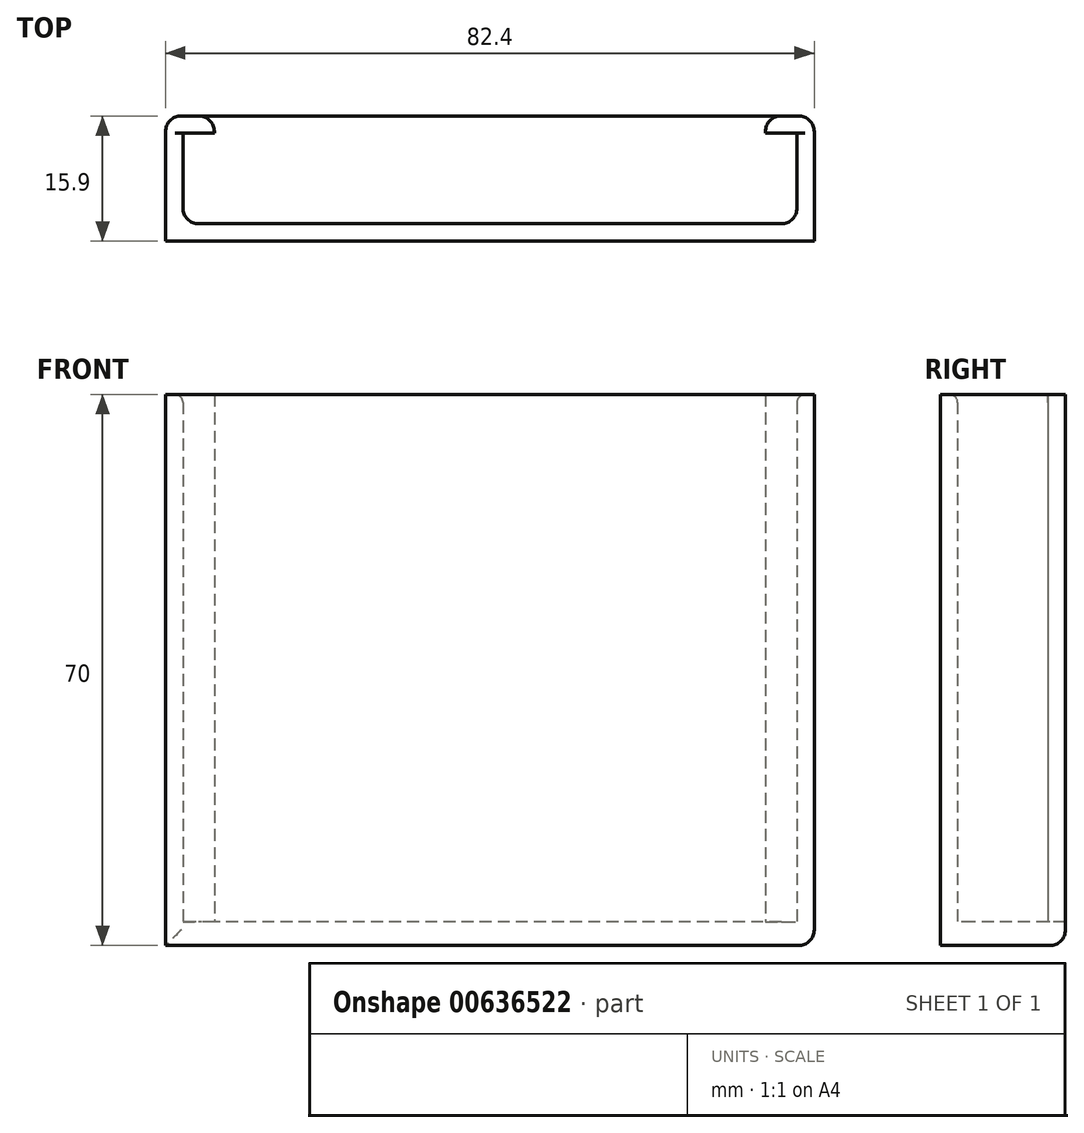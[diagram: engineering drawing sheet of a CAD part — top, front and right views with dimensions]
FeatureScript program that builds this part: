
annotation { "Feature Type Name" : "Feature", "Feature Type Description" : "" }
export const myFeature = defineFeature(function(context is Context, id is Id, definition is map)
    precondition{}
    {
        {
            var Q0;
            Q0=qCreatedBy(makeId("Top.planeOp"),FACE);
            var sketch = newSketch(context, id + "F0", { "sketchPlane" : qUnion([Q0])});
            skLineSegment(sketch, "E0", {"start": v(0, 7.22) * mm, "end": v(0, -7.47) * mm, "construction": true});
            skLineSegment(sketch, "E1", {"start": v(0, 0) * mm, "end": v(41.2, 0) * mm});
            skLineSegment(sketch, "E2", {"start": v(41.2, 0) * mm, "end": v(41.2, 15.9) * mm});
            skLineSegment(sketch, "E3", {"start": v(41.2, 15.9) * mm, "end": v(35, 15.9) * mm});
            skLineSegment(sketch, "E4", {"start": v(0, 2.2) * mm, "end": v(0, 0) * mm});
            skLineSegment(sketch, "E5.MirrorCS", {"start": v(-41.2, 0) * mm, "end": v(-41.2, 15.9) * mm});
            skLineSegment(sketch, "E6.MirrorCS", {"start": v(0, 0) * mm, "end": v(-41.2, 0) * mm});
            skLineSegment(sketch, "E7", {"start": v(35, 15.9) * mm, "end": v(35, 13.7) * mm});
            skLineSegment(sketch, "E8", {"start": v(35, 13.7) * mm, "end": v(39, 13.7) * mm});
            skLineSegment(sketch, "E9", {"start": v(39, 13.7) * mm, "end": v(39, 2.2) * mm});
            skLineSegment(sketch, "E10", {"start": v(39, 2.2) * mm, "end": v(0, 2.2) * mm});
            skLineSegment(sketch, "E11.MirrorCS", {"start": v(-39, 2.2) * mm, "end": v(0, 2.2) * mm});
            skLineSegment(sketch, "E12.MirrorCS", {"start": v(-39, 13.7) * mm, "end": v(-39, 2.2) * mm});
            skLineSegment(sketch, "E13.MirrorCS", {"start": v(-35, 13.7) * mm, "end": v(-39, 13.7) * mm});
            skLineSegment(sketch, "E14.MirrorCS", {"start": v(-35, 15.9) * mm, "end": v(-35, 13.7) * mm});
            skLineSegment(sketch, "E15.MirrorCS", {"start": v(-41.2, 15.9) * mm, "end": v(-35, 15.9) * mm});
            skLineSegment(sketch, "E16.top", {"start": v(-41.2, 0) * mm, "end": v(41.2, 0) * mm});
            skLineSegment(sketch, "E16.left", {"start": v(-41.2, 15.9) * mm, "end": v(-41.2, 0) * mm});
            skLineSegment(sketch, "E16.right", {"start": v(41.2, 14.6) * mm, "end": v(41.2, 0) * mm});
            skSolve(sketch);
        }
        {
            var Q0;
            Q0=makeQuery(id+"F0.imprint","IMPRINT",FACE,{"disambiguationData":[TD([[makeQuery(id+"F0.imprint","IMPRINT",EDGE,{"derivedFrom":sQuery(id+"F0.wireOp",EDGE,"E4")}),-1.0]])]});
            var Q1;
            Q1=makeQuery(id+"F0.imprint","IMPRINT",FACE,{"disambiguationData":[TD([[makeQuery(id+"F0.imprint","IMPRINT",EDGE,{"derivedFrom":sQuery(id+"F0.wireOp",EDGE,"E1")}),1.0]])]});
            var Q2;
            {var subQ1=sQuery(id+"F0.wireOp",EDGE,"E4");Q2=makeQuery(id+"F0.imprint","IMPRINT",FACE,{"disambiguationData":[TD([[makeQuery(id+"F0.imprint","IMPRINT",EDGE,{"derivedFrom":subQ1}),1.0]])]});}
            extrude(context, id + "F1", {"entities" : qUnion([Q0, Q1, Q2]), "depth" : 70 * mm});
        }
        {
            var Q0;
            {var subQ0=sQuery(id+"F0.wireOp",EDGE,"E4");Q0=makeQuery(id+"F0.imprint","IMPRINT",FACE,{"disambiguationData":[TD([[makeQuery(id+"F0.imprint","IMPRINT",EDGE,{"derivedFrom":subQ0}),-1.0]])]});}
            var sketch = newSketch(context, id + "F2", { "sketchPlane" : qUnion([Q0])});
            skLineSegment(sketch, "E17.bottom", {"start": v(41.2, 0) * mm, "end": v(-41.2, 0) * mm});
            skLineSegment(sketch, "E17.top", {"start": v(41.2, 15.9) * mm, "end": v(-41.2, 15.9) * mm});
            skLineSegment(sketch, "E17.left", {"start": v(41.2, 0) * mm, "end": v(41.2, 15.9) * mm});
            skLineSegment(sketch, "E17.right", {"start": v(-41.2, 0) * mm, "end": v(-41.2, 15.9) * mm});
            skSolve(sketch);
        }
        {
            var Q0;
            {var subQ1=sQuery(id+"F2.wireOp",EDGE,"E17.left");Q0=makeQuery(id+"F2.imprint","IMPRINT",FACE,{"disambiguationData":[TD([[makeQuery(id+"F2.imprint","IMPRINT",EDGE,{"derivedFrom":subQ1}),1.0]])]});}
            var Q1;
            {var subQ1=sQuery(id+"F2.wireOp",EDGE,"E17.right");Q1=makeQuery(id+"F2.imprint","IMPRINT",FACE,{"disambiguationData":[TD([[makeQuery(id+"F2.imprint","IMPRINT",EDGE,{"derivedFrom":subQ1}),1.0]])]});}
            extrude(context, id + "F3", {"entities" : qUnion([Q0, Q1]), "operationType" : NewBodyOperationType.ADD, "depth" : 3 * mm});
        }
        {
            var Q0;
            Q0=makeQuery(id+"F1.opExtrude","SWEPT_EDGE",EDGE,{"disambiguationData":[OSD([sQuery(id+"F0.wireOp",EDGE,"E16.top"),sQuery(id+"F0.wireOp",EDGE,"E16.right")])]});
            var Q1;
            Q1=makeQuery(id+"F1.opExtrude","SWEPT_EDGE",EDGE,{"disambiguationData":[OSD([sQuery(id+"F0.wireOp",EDGE,"E2"),sQuery(id+"F0.wireOp",EDGE,"E3")])]});
            var Q2;
            Q2=makeQuery(id+"F1.opExtrude","SWEPT_EDGE",EDGE,{"disambiguationData":[OSD([sQuery(id+"F0.wireOp",EDGE,"E3"),sQuery(id+"F0.wireOp",EDGE,"E7")])]});
            var Q3;
            Q3=makeQuery(id+"F1.opExtrude","SWEPT_EDGE",EDGE,{"disambiguationData":[OSD([sQuery(id+"F0.wireOp",EDGE,"E9"),sQuery(id+"F0.wireOp",EDGE,"E10")])]});
            var Q4;
            Q4=makeQuery(id+"F1.opExtrude","SWEPT_EDGE",EDGE,{"disambiguationData":[OSD([sQuery(id+"F0.wireOp",EDGE,"E14.MirrorCS"),sQuery(id+"F0.wireOp",EDGE,"E15.MirrorCS")])]});
            var Q5;
            Q5=makeQuery(id+"F1.opExtrude","SWEPT_EDGE",EDGE,{"disambiguationData":[OSD([sQuery(id+"F0.wireOp",EDGE,"E11.MirrorCS"),sQuery(id+"F0.wireOp",EDGE,"E12.MirrorCS")])]});
            var Q6;
            Q6=makeQuery(id+"F1.opExtrude","SWEPT_EDGE",EDGE,{"disambiguationData":[OSD([sQuery(id+"F0.wireOp",EDGE,"E15.MirrorCS"),sQuery(id+"F0.wireOp",EDGE,"E16.left")])]});
            var Q7;
            Q7=makeQuery(id+"F1.opExtrude","SWEPT_EDGE",EDGE,{"disambiguationData":[OSD([sQuery(id+"F0.wireOp",EDGE,"E16.top"),sQuery(id+"F0.wireOp",EDGE,"E16.left")])]});
            var Q8;
            Q8=makeQuery(id+"F1.opExtrude","CAP_EDGE",EDGE,{"disambiguationData":[OSD([sQuery(id+"F0.wireOp",EDGE,"E16.top")])],"isStart":true});
            var Q9;
            Q9=makeQuery(id+"F3.boolean.opBoolean","MERGE",EDGE,{"derivedFrom":[makeQuery(id+"F1.opExtrude","CAP_EDGE",EDGE,{"disambiguationData":[OSD([sQuery(id+"F0.wireOp",EDGE,"E3")])],"isStart":true}),makeQuery(id+"F1.opExtrude","CAP_EDGE",EDGE,{"disambiguationData":[OSD([sQuery(id+"F0.wireOp",EDGE,"E15.MirrorCS")])],"isStart":true}),makeQuery(id+"F3.opExtrude","CAP_EDGE",EDGE,{"disambiguationData":[OSD([sQuery(id+"F2.wireOp",EDGE,"E17.top")])],"isStart":true})]});
            var Q10;
            Q10=makeQuery(id+"F1.opExtrude","CAP_EDGE",EDGE,{"disambiguationData":[OSD([sQuery(id+"F0.wireOp",EDGE,"E16.left")])],"isStart":true});
            var Q11;
            Q11=makeQuery(id+"F1.opExtrude","CAP_EDGE",EDGE,{"disambiguationData":[OSD([sQuery(id+"F0.wireOp",EDGE,"E2"),sQuery(id+"F0.wireOp",EDGE,"E16.right")])],"isStart":true});
            fillet(context, id + "F4", {"entities" : qUnion([Q0, Q1, Q2, Q3, Q4, Q5, Q6, Q7, Q8, Q9, Q10, Q11]), "radius" : 2 * mm, "tangentPropagation" : true, "allowEdgeOverflow" : false});
        }
        {
            var Q0;
            Q0=makeQuery(id+"F1.opExtrude","CAP_EDGE",EDGE,{"disambiguationData":[OSD([sQuery(id+"F0.wireOp",EDGE,"E10"),sQuery(id+"F0.wireOp",EDGE,"E11.MirrorCS")])],"isStart":false});
            var Q1;
            Q1=makeQuery(id+"F1.opExtrude","CAP_EDGE",EDGE,{"disambiguationData":[OSD([sQuery(id+"F0.wireOp",EDGE,"E16.top")])],"isStart":false});
            fillet(context, id + "F5", {"entities" : qUnion([Q0, Q1]), "radius" : 1 * mm, "tangentPropagation" : true, "allowEdgeOverflow" : false});
        }
    });
